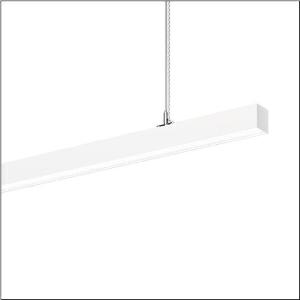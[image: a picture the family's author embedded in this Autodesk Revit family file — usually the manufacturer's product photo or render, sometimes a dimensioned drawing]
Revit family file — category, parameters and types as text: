
# Revit family: silica_r__21_51mx33db39wb_e509
name_source: partatom
category: Lighting Fixtures
units: mm (PartAtom-declared; Revit-internal decimal feet)

## family parameters
Cut with Voids When Loaded = No
Host = Face
Light Source = No
Part Type = Normal
Room Calculation Point = No
Round Connector Dimension = Use Diameter
Shared = No

## types (1)
- --- (1 x LED, 7390 lm, 51.6 W, 3000K)
    Apparent Load = 52 VA
    CIE Flux Codes = 78 96 99 55 100
    Color Rendering = 80
    Color Temperature = 3000K
    Default Elevation = 1800 mm
    Description = Silica® 21, office luminaire, primary optical cover: prismatic diffuser, of PMMA, CAT 2 (L<= 3000cd/m²), light emission: direct/indirect distribution, primary light characteristic: symmetric, installation type: suspended mounting, LED, rated luminous flux: 7.390lm, luminous efficacy: 143lm/W, light colour: 830, colour temperature: 3000K, with terminal, 3+2-pole, max. 2.5mm², mains connection: 220..240V, AC, 50/60Hz, rated input power: 51.6W, luminaire housing, of aluminium, traffic white (RAL 9016), length: 1.504mm, width: 53mm, height: 53mm, protection rating (complete): IP20, insulation class (complete): insulation class I (protective earthing), certification: CE, permissible operating ambient temperature: 0..+35°C, standard: EN 50419, packaging unit: 1 piece
    Height = 53 mm
    Lamp = 1 x LED
    Lamp Light Flux = 7390 lm
    Lamp Power = 51.6 W
    Lamp count = 1
    Length = 1504 mm
    Luminous efficacy = 143 lm/W
    Manufacturer = Siteco
    ModVariant = No
    Model = 51MX33DB39WB
    Mounting Place = Ceiling
    Mounting Type = Pendant
    Number of Poles = 1
    OnlyDefault = Yes
    Power Factor = 1
    Product Name = Silica® 21
    Product group = office luminaire | ceiling pendant
    ProductGroupID = 902
    Protection Class = Protection class I
    Protection Degree = IP 20
    RLX_Detail_Level = 1
    RLX_Emergency_Light_Flux = 0 lm
    RLX_Emergency_Type = 0
    RLX_Emergency_Type_DB = No
    RlxData = <blob elided: 21397 chars, md5=1489e71f>
    Socket = socket
    Standby Power = 0 W
    System Light Flux = 7390 lm
    System Power = 52 W
    Type Comments = factory setting: luminous flux: 100 % | dim-lin: 254 | 345 mA
    Type Image = l_1313629.jpg
    URL = http://relux.com
    VarID = @adj_066769
    Voltage = 0 V
    Weight = 0.00 kg
    Width = 53 mm

## geometry (parser evidence)
native form markers: Blend x4, Sweep x12
no freeform markers — native parametric forms only
